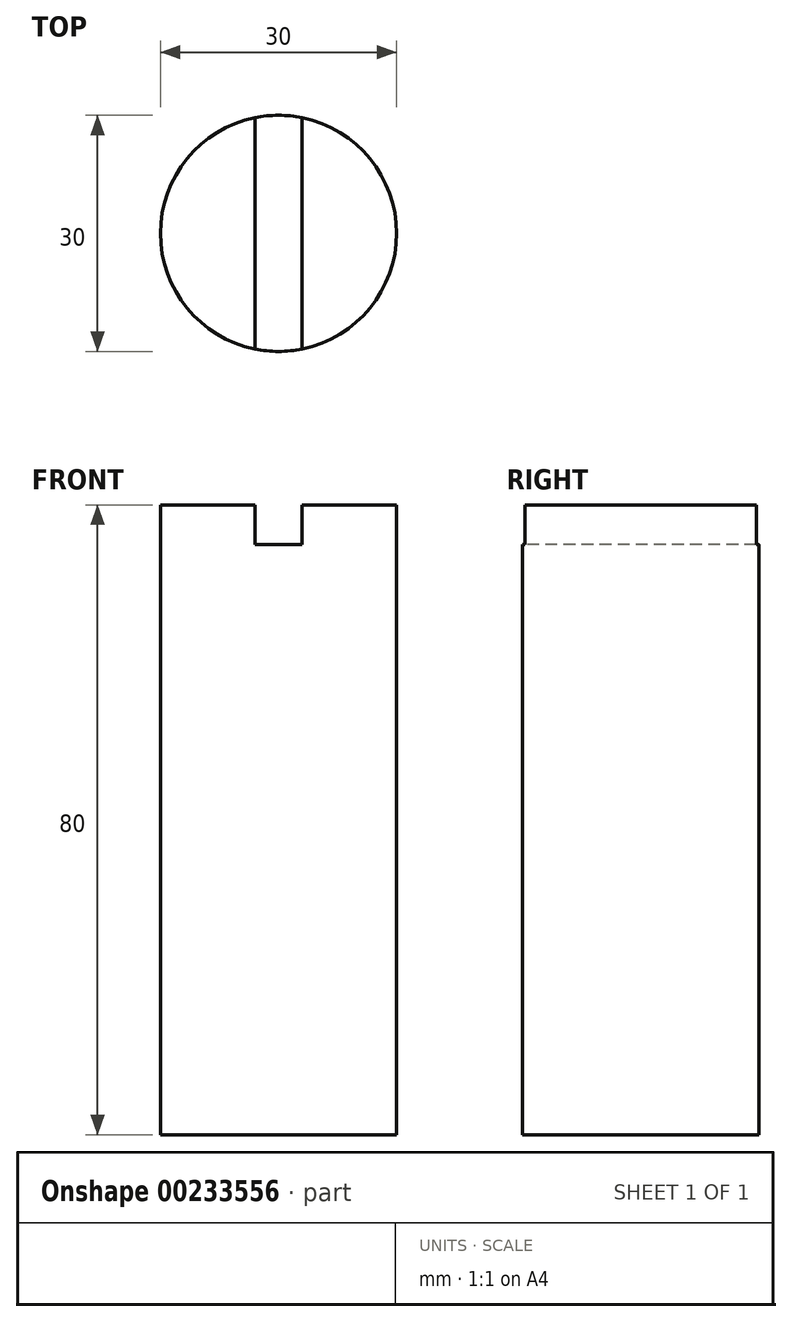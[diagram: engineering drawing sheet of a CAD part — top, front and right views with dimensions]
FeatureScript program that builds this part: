
annotation { "Feature Type Name" : "Feature", "Feature Type Description" : "" }
export const myFeature = defineFeature(function(context is Context, id is Id, definition is map)
    precondition{}
    {
        {
            var Q0;
            Q0=qCreatedBy(makeId("Front.planeOp"),FACE);
            var sketch = newSketch(context, id + "F0", { "sketchPlane" : qUnion([Q0])});
            skLineSegment(sketch, "E0", {"start": v(0, 0) * mm, "end": v(0, 80) * mm});
            skLineSegment(sketch, "E1", {"start": v(0, 80) * mm, "end": v(-15, 80) * mm});
            skLineSegment(sketch, "E2", {"start": v(-15, 80) * mm, "end": v(-15, 0) * mm});
            skLineSegment(sketch, "E3", {"start": v(-15, 0) * mm, "end": v(0, 0) * mm});
            skSolve(sketch);
        }
        {
            var Q0;
            Q0=makeQuery(id+"F0.imprint","IMPRINT",FACE,{"disambiguationData":[TD([[makeQuery(id+"F0.imprint","IMPRINT",EDGE,{"derivedFrom":sQuery(id+"F0.wireOp",EDGE,"E0")}),1.0]])]});
            var Q1;
            Q1=sQuery(id+"F0.wireOp",EDGE,"E0");
            revolve(context, id + "F1", {"entities" : qUnion([Q0]), "axis" : qUnion([Q1]), "revolveType" : RevolveType.FULL});
        }
        {
            var Q0;
            Q0=makeQuery(id+"F1.opRevolve","SWEPT_FACE",FACE,{"disambiguationData":[OSD([sQuery(id+"F0.wireOp",EDGE,"E1")])]});
            var sketch = newSketch(context, id + "F2", { "sketchPlane" : qUnion([Q0])});
            skLineSegment(sketch, "E4", {"start": v(-3, 14.7) * mm, "end": v(-3, -14.7) * mm});
            skLineSegment(sketch, "E5", {"start": v(3, 14.7) * mm, "end": v(3, -14.7) * mm});
            skSolve(sketch);
        }
        {
            var Q0;
            {var subQ0=sQuery(id+"F2.wireOp",EDGE,"E4");Q0=makeQuery(id+"F2.imprint","IMPRINT",FACE,{"disambiguationData":[TD([[makeQuery(id+"F2.imprint","IMPRINT",EDGE,{"derivedFrom":subQ0}),1.0]])]});}
            extrude(context, id + "F3", {"entities" : qUnion([Q0]), "operationType" : NewBodyOperationType.REMOVE, "oppositeDirection" : true, "depth" : 5 * mm});
        }
    });
